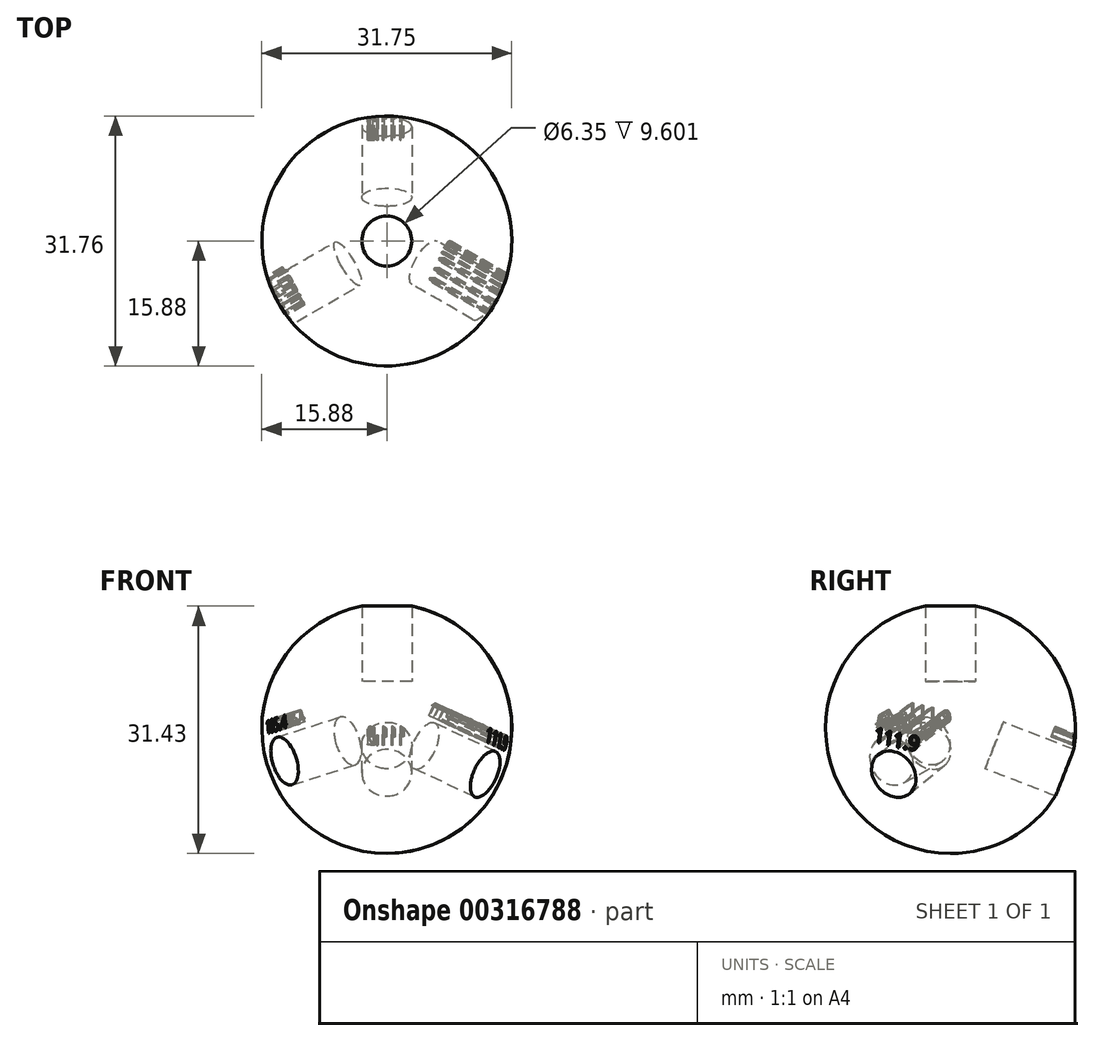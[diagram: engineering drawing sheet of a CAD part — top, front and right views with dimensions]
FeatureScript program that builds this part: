
annotation { "Feature Type Name" : "Feature", "Feature Type Description" : "" }
export const myFeature = defineFeature(function(context is Context, id is Id, definition is map)
    precondition{}
    {
        {
            var Q0;
            Q0=qCreatedBy(makeId("Front.planeOp"),FACE);
            var sketch = newSketch(context, id + "F0", { "sketchPlane" : qUnion([Q0])});
            skArc(sketch, "E0", {"start": v(0, 15.88) * mm, "mid": v(-15.88, 0) * mm, "end": v(0, -15.88) * mm});
            skLineSegment(sketch, "E1", {"start": v(0, 15.88) * mm, "end": v(0, -15.88) * mm});
            skSolve(sketch);
        }
        {
            var Q0;
            Q0 = qSketchRegion(id + "F0", true);
            var Q1;
            Q1=sQuery(id+"F0.wireOp",EDGE,"E1");
            revolve(context, id + "F1", {"entities" : qUnion([Q0]), "axis" : qUnion([Q1]), "revolveType" : RevolveType.FULL});
        }
        {
            var Q0;
            Q0=qCreatedBy(makeId("Top.planeOp"),FACE);
            cPlane(context, id + "F2", {"entities" : qUnion([Q0]), "cplaneType" : CPlaneType.OFFSET, "offset" : 5.95 * mm, "width" : 152.4 * mm, "height" : 152.4 * mm});
        }
        {
            var Q0;
            Q0=qCreatedBy(id+"F2.planeOp",FACE);
            var sketch = newSketch(context, id + "F3", { "sketchPlane" : qUnion([Q0])});
            skCircle(sketch, "E2", {"center": v(0, 0) * mm, "radius": 3.18 * mm});
            skSolve(sketch);
        }
        {
            var Q0;
            Q0 = qSketchRegion(id + "F3", true);
            var Q1;
            Q1=sQuery(id+"F3.wireOp",EDGE,"E2");
            extrude(context, id + "F4", {"entities" : qUnion([Q0]), "surfaceEntities" : qUnion([Q1]), "depth" : 25.4 * mm});
        }
        {
            var Q0;
            Q0 = qSketchRegion(id + "F3", true);
            var Q1;
            Q1=sQuery(id+"F3.wireOp",EDGE,"E2");
            extrude(context, id + "F5", {"entities" : qUnion([Q0]), "surfaceEntities" : qUnion([Q1]), "depth" : 25.4 * mm});
        }
        {
            var Q0;
            Q0=makeQuery(id+"F4.opExtrude","SWEPT_BODY",BODY,{"disambiguationData":[OSD([sQuery(id+"F3.wireOp",EDGE,"E2")])]});
            deleteBodies(context, id + "F6", {"entities" : qUnion([Q0])});
        }
        {
            var Q0;
            Q0=qCreatedBy(makeId("Front.planeOp"),FACE);
            var sketch = newSketch(context, id + "F7", { "sketchPlane" : qUnion([Q0])});
            skLineSegment(sketch, "E3", {"start": v(0, 0) * mm, "end": v(0, 35.52) * mm, "construction": true});
            skSolve(sketch);
        }
        {
            var Q0;
            Q0=qCreatedBy(makeId("Top.planeOp"),FACE);
            var sketch = newSketch(context, id + "F8", { "sketchPlane" : qUnion([Q0])});
            skLineSegment(sketch, "E4", {"start": v(0, 0) * mm, "end": v(-35.28, 0) * mm, "construction": true});
            skLineSegment(sketch, "E5", {"start": v(0, 0) * mm, "end": v(0, -34.62) * mm, "construction": true});
            skLineSegment(sketch, "E6", {"start": v(0, 0) * mm, "end": v(29.6, 0) * mm, "construction": true});
            skSolve(sketch);
        }
        {
            var Q0;
            Q0=makeQuery(id+"F5.opExtrude","SWEPT_BODY",BODY,{"disambiguationData":[OSD([sQuery(id+"F3.wireOp",EDGE,"E2")])]});
            var Q1;
            Q1=sQuery(id+"F8.wireOp",EDGE,"E4");
            transform(context, id + "F9", {"entities" : qUnion([Q0]), "transformType" : TransformType.ROTATION, "transformAxis" : qUnion([Q1]), "angle" : 111.2 * degree, "makeCopy" : true});
        }
        {
            var Q0;
            Q0=makeQuery(id+"F5.opExtrude","SWEPT_BODY",BODY,{"disambiguationData":[OSD([sQuery(id+"F3.wireOp",EDGE,"E2")])]});
            var Q1;
            Q1=sQuery(id+"F8.wireOp",EDGE,"E5");
            transform(context, id + "F10", {"entities" : qUnion([Q0]), "transformType" : TransformType.ROTATION, "transformAxis" : qUnion([Q1]), "angle" : 105.4 * degree, "makeCopy" : true});
        }
        {
            var Q0;
            Q0=makeQuery(id+"F10.opPattern","COPY",BODY,{"derivedFrom":makeQuery(id+"F5.opExtrude","SWEPT_BODY",BODY,{"disambiguationData":[OSD([sQuery(id+"F3.wireOp",EDGE,"E2")])]}),"instanceName":"1"});
            var Q1;
            Q1=sQuery(id+"F7.wireOp",EDGE,"E3");
            transform(context, id + "F11", {"entities" : qUnion([Q0]), "transformType" : TransformType.ROTATION, "transformAxis" : qUnion([Q1]), "angle" : 30 * degree, "makeCopy" : false});
        }
        {
            var Q0;
            Q0=makeQuery(id+"F5.opExtrude","SWEPT_BODY",BODY,{"disambiguationData":[OSD([sQuery(id+"F3.wireOp",EDGE,"E2")])]});
            var Q1;
            Q1=sQuery(id+"F8.wireOp",EDGE,"E6");
            transform(context, id + "F12", {"entities" : qUnion([Q0]), "transformType" : TransformType.ROTATION, "transformAxis" : qUnion([Q1]), "angle" : 111.9 * degree, "makeCopy" : true});
        }
        {
            var Q0;
            Q0=makeQuery(id+"F12.opPattern","COPY",BODY,{"derivedFrom":makeQuery(id+"F5.opExtrude","SWEPT_BODY",BODY,{"disambiguationData":[OSD([sQuery(id+"F3.wireOp",EDGE,"E2")])]}),"instanceName":"1"});
            var Q1;
            Q1=sQuery(id+"F7.wireOp",EDGE,"E3");
            transform(context, id + "F13", {"entities" : qUnion([Q0]), "transformType" : TransformType.ROTATION, "transformAxis" : qUnion([Q1]), "angle" : 60 * degree, "makeCopy" : false});
        }
        {
            var Q0;
            Q0=makeQuery(id+"F12.opPattern","COPY",FACE,{"derivedFrom":makeQuery(id+"F5.opExtrude","CAP_FACE",FACE,{"disambiguationData":[OSD([sQuery(id+"F3.wireOp",EDGE,"E2")])],"isStart":false}),"instanceName":"1"});
            cPlane(context, id + "F14", {"entities" : qUnion([Q0]), "cplaneType" : CPlaneType.OFFSET, "offset" : 12.7 * mm, "oppositeDirection" : true, "width" : 152.4 * mm, "height" : 152.4 * mm});
        }
        {
            var Q0;
            Q0=qCreatedBy(id+"F14.planeOp",FACE);
            var sketch = newSketch(context, id + "F15", { "sketchPlane" : qUnion([Q0])});
            skText(sketch, "E7", { "text": "111.9", "fontName": "OpenSans-Regular.ttf"});
            const initialGuessF15  = {"E7": [-0.00305, 0.00377, 1, 0, 0.00178]};
            skSetInitialGuess(sketch, initialGuessF15);
            skSolve(sketch);
        }
        {
            var Q0;
            Q0 = qSketchRegion(id + "F15", true);
            extrude(context, id + "F16", {"entities" : qUnion([Q0]), "operationType" : NewBodyOperationType.REMOVE, "oppositeDirection" : true, "depth" : 12.7 * mm});
        }
        {
            var Q0;
            Q0=makeQuery(id+"F9.opPattern","COPY",FACE,{"derivedFrom":makeQuery(id+"F5.opExtrude","CAP_FACE",FACE,{"disambiguationData":[OSD([sQuery(id+"F3.wireOp",EDGE,"E2")])],"isStart":false}),"instanceName":"1"});
            cPlane(context, id + "F17", {"entities" : qUnion([Q0]), "cplaneType" : CPlaneType.OFFSET, "offset" : 12.7 * mm, "oppositeDirection" : true, "width" : 152.4 * mm, "height" : 152.4 * mm});
        }
        {
            var Q0;
            Q0=qCreatedBy(id+"F17.planeOp",FACE);
            var sketch = newSketch(context, id + "F18", { "sketchPlane" : qUnion([Q0])});
            skText(sketch, "E8", { "text": "111.2", "fontName": "OpenSans-Regular.ttf"});
            const initialGuessF18  = {"E8": [-0.00235, 0.00367, 1, 0, 0.00139]};
            skSetInitialGuess(sketch, initialGuessF18);
            skSolve(sketch);
        }
        {
            var Q0;
            Q0 = qSketchRegion(id + "F18", true);
            extrude(context, id + "F19", {"entities" : qUnion([Q0]), "operationType" : NewBodyOperationType.REMOVE, "oppositeDirection" : true, "depth" : 6.35 * mm});
        }
        {
            var Q0;
            Q0=makeQuery(id+"F10.opPattern","COPY",FACE,{"derivedFrom":makeQuery(id+"F5.opExtrude","CAP_FACE",FACE,{"disambiguationData":[OSD([sQuery(id+"F3.wireOp",EDGE,"E2")])],"isStart":false}),"instanceName":"1"});
            cPlane(context, id + "F20", {"entities" : qUnion([Q0]), "cplaneType" : CPlaneType.OFFSET, "offset" : 12.7 * mm, "oppositeDirection" : true, "width" : 152.4 * mm, "height" : 152.4 * mm});
        }
        {
            var Q0;
            Q0=qCreatedBy(id+"F20.planeOp",FACE);
            var sketch = newSketch(context, id + "F21", { "sketchPlane" : qUnion([Q0])});
            skText(sketch, "E9", { "text": "105.4", "fontName": "OpenSans-Regular.ttf"});
            const initialGuessF21  = {"E9": [-0.00317, 0.00395, 1, 0, 0.00162]};
            skSetInitialGuess(sketch, initialGuessF21);
            skSolve(sketch);
        }
        {
            var Q0;
            Q0 = qSketchRegion(id + "F21", true);
            extrude(context, id + "F22", {"entities" : qUnion([Q0]), "operationType" : NewBodyOperationType.REMOVE, "oppositeDirection" : true, "depth" : 6.35 * mm});
        }
        {
            var Q0;
            Q0=makeQuery(id+"F12.opPattern","COPY",BODY,{"derivedFrom":makeQuery(id+"F5.opExtrude","SWEPT_BODY",BODY,{"disambiguationData":[OSD([sQuery(id+"F3.wireOp",EDGE,"E2")])]}),"instanceName":"1"});
            var Q1;
            Q1=makeQuery(id+"F10.opPattern","COPY",BODY,{"derivedFrom":makeQuery(id+"F5.opExtrude","SWEPT_BODY",BODY,{"disambiguationData":[OSD([sQuery(id+"F3.wireOp",EDGE,"E2")])]}),"instanceName":"1"});
            var Q2;
            Q2=makeQuery(id+"F9.opPattern","COPY",BODY,{"derivedFrom":makeQuery(id+"F5.opExtrude","SWEPT_BODY",BODY,{"disambiguationData":[OSD([sQuery(id+"F3.wireOp",EDGE,"E2")])]}),"instanceName":"1"});
            var Q3;
            Q3=makeQuery(id+"F1.opRevolve","SWEPT_BODY",BODY,{"disambiguationData":[OSD([sQuery(id+"F0.wireOp",EDGE,"E0"),sQuery(id+"F0.wireOp",EDGE,"E1")])]});
            booleanBodies(context, id + "F23", {"operationType" : BooleanOperationType.SUBTRACTION, "tools" : qUnion([Q0, Q1, Q2]), "targets" : qUnion([Q3])});
        }
        {
            var Q0;
            Q0=makeQuery(id+"F5.opExtrude","SWEPT_BODY",BODY,{"disambiguationData":[OSD([sQuery(id+"F3.wireOp",EDGE,"E2")])]});
            var Q1;
            Q1=makeQuery(id+"F1.opRevolve","SWEPT_BODY",BODY,{"disambiguationData":[OSD([sQuery(id+"F0.wireOp",EDGE,"E0"),sQuery(id+"F0.wireOp",EDGE,"E1")])]});
            booleanBodies(context, id + "F24", {"operationType" : BooleanOperationType.SUBTRACTION, "tools" : qUnion([Q0]), "targets" : qUnion([Q1])});
        }
    });
